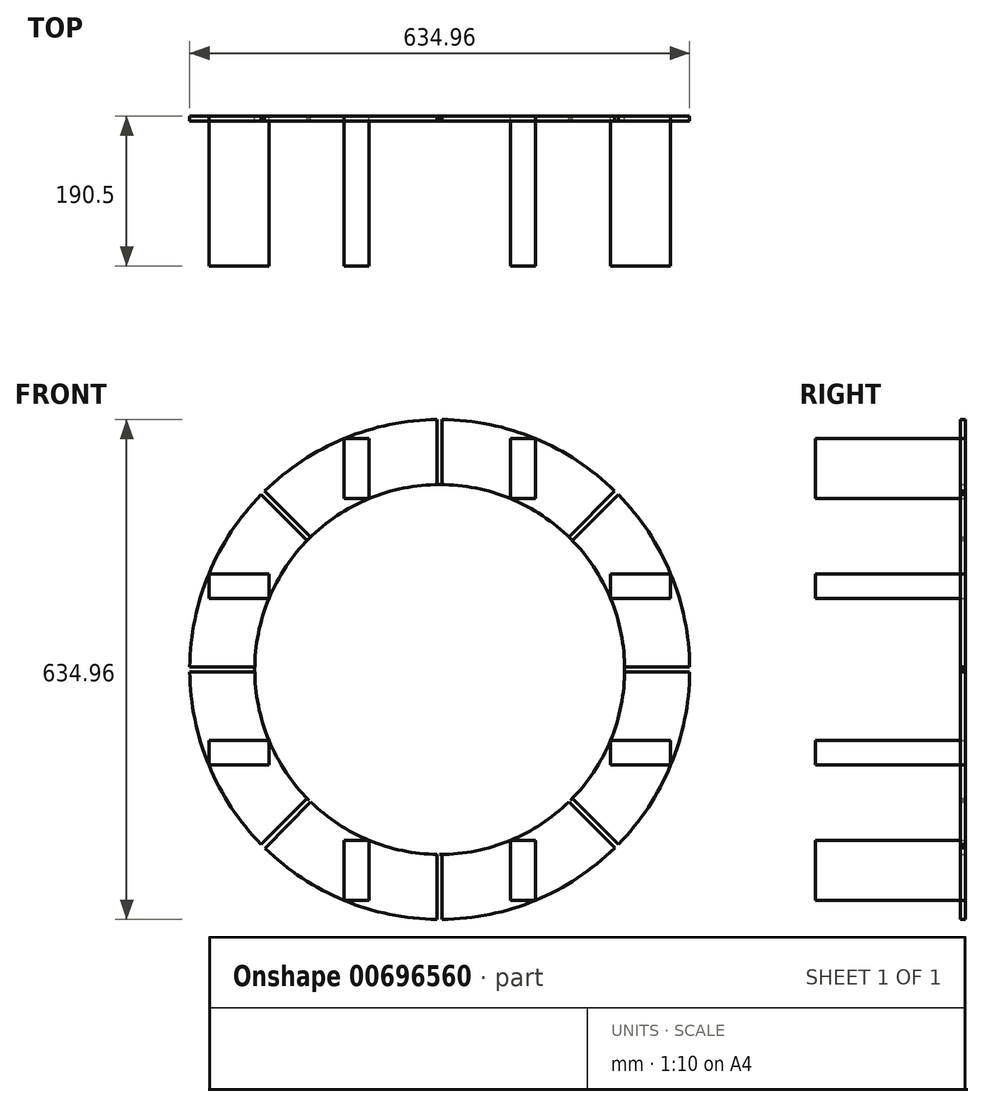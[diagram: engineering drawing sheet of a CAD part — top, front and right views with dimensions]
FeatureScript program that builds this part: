
annotation { "Feature Type Name" : "Feature", "Feature Type Description" : "" }
export const myFeature = defineFeature(function(context is Context, id is Id, definition is map)
    precondition{}
    {
        {
            var Q0;
            Q0=qCreatedBy(makeId("Front.planeOp"),FACE);
            var sketch = newSketch(context, id + "F0", { "sketchPlane" : qUnion([Q0])});
            skCircle(sketch, "E0", {"center": v(0, 0) * mm, "radius": 234.95 * mm});
            skCircle(sketch, "E1", {"center": v(0, 0) * mm, "radius": 317.5 * mm});
            skLineSegment(sketch, "E2", {"start": v(317.48, 0) * mm, "end": v(317.5, 0) * mm});
            skLineSegment(sketch, "E3", {"start": v(317.5, 0) * mm, "end": v(317.48, 0) * mm});
            skLineSegment(sketch, "E4", {"start": v(-317.48, 0) * mm, "end": v(-317.5, 0) * mm});
            skLineSegment(sketch, "E5", {"start": v(0, 317.5) * mm, "end": v(0, 317.5) * mm});
            skLineSegment(sketch, "E6", {"start": v(0, -317.48) * mm, "end": v(0, -317.5) * mm});
            skLineSegment(sketch, "E7.bottom", {"start": v(-317.5, 0) * mm, "end": v(-317.48, 0) * mm});
            skLineSegment(sketch, "E8", {"start": v(-224.5, 224.5) * mm, "end": v(-224.5, 224.5) * mm});
            skLineSegment(sketch, "E9", {"start": v(224.5, 224.5) * mm, "end": v(224.5, 224.5) * mm});
            skLineSegment(sketch, "E10", {"start": v(-224.5, -224.5) * mm, "end": v(-224.5, -224.5) * mm});
            skLineSegment(sketch, "E11", {"start": v(224.5, -224.5) * mm, "end": v(224.5, -224.5) * mm});
            skLineSegment(sketch, "E12", {"start": v(-166.13, -166.13) * mm, "end": v(-163.87, -168.36) * mm});
            skLineSegment(sketch, "E13", {"start": v(-166.13, -166.13) * mm, "end": v(-168.38, -163.89) * mm});
            skLineSegment(sketch, "E14", {"start": v(-168.38, -163.89) * mm, "end": v(-226.74, -222.25) * mm});
            skLineSegment(sketch, "E15", {"start": v(-163.87, -168.36) * mm, "end": v(-221.85, -227.13) * mm});
            skLineSegment(sketch, "E16", {"start": v(-221.85, -227.13) * mm, "end": v(-226.74, -222.25) * mm});
            skLineSegment(sketch, "E17", {"start": v(0, -234.95) * mm, "end": v(-3.17, -234.93) * mm});
            skLineSegment(sketch, "E18", {"start": v(0, -234.95) * mm, "end": v(3.18, -234.95) * mm});
            skLineSegment(sketch, "E19", {"start": v(-3.17, -234.93) * mm, "end": v(-3.17, -317.48) * mm});
            skLineSegment(sketch, "E20", {"start": v(3.18, -234.95) * mm, "end": v(3.18, -317.48) * mm});
            skLineSegment(sketch, "E21", {"start": v(3.18, -317.48) * mm, "end": v(-3.17, -317.48) * mm});
            skLineSegment(sketch, "E22", {"start": v(166.13, -166.13) * mm, "end": v(163.74, -168.22) * mm});
            skLineSegment(sketch, "E23", {"start": v(166.13, -166.13) * mm, "end": v(168.38, -163.89) * mm});
            skLineSegment(sketch, "E24", {"start": v(163.74, -168.22) * mm, "end": v(222.26, -226.73) * mm});
            skLineSegment(sketch, "E25", {"start": v(168.38, -163.89) * mm, "end": v(226.74, -222.25) * mm});
            skLineSegment(sketch, "E26", {"start": v(226.74, -222.25) * mm, "end": v(222.26, -226.73) * mm});
            skLineSegment(sketch, "E27", {"start": v(234.95, 0) * mm, "end": v(234.95, -3.17) * mm});
            skLineSegment(sketch, "E28", {"start": v(234.95, 0) * mm, "end": v(234.95, 3.18) * mm});
            skLineSegment(sketch, "E29", {"start": v(234.95, 3.18) * mm, "end": v(317.48, 3.18) * mm});
            skLineSegment(sketch, "E30", {"start": v(317.48, 3.18) * mm, "end": v(317.48, -3.18) * mm});
            skLineSegment(sketch, "E31", {"start": v(317.48, -3.18) * mm, "end": v(234.95, -3.17) * mm});
            skLineSegment(sketch, "E32", {"start": v(166.13, 166.13) * mm, "end": v(168.38, 163.89) * mm});
            skLineSegment(sketch, "E33", {"start": v(166.13, 166.13) * mm, "end": v(163.89, 168.38) * mm});
            skLineSegment(sketch, "E34", {"start": v(168.38, 163.89) * mm, "end": v(226.74, 222.25) * mm});
            skLineSegment(sketch, "E35", {"start": v(226.74, 222.25) * mm, "end": v(222.25, 226.74) * mm});
            skLineSegment(sketch, "E36", {"start": v(222.25, 226.74) * mm, "end": v(163.89, 168.38) * mm});
            skLineSegment(sketch, "E37", {"start": v(0, 234.95) * mm, "end": v(3.17, 234.95) * mm});
            skLineSegment(sketch, "E38", {"start": v(0, 234.95) * mm, "end": v(-3.17, 234.95) * mm});
            skLineSegment(sketch, "E39", {"start": v(-3.17, 234.95) * mm, "end": v(-3.17, 317.48) * mm});
            skLineSegment(sketch, "E40", {"start": v(-3.17, 317.48) * mm, "end": v(3.17, 317.5) * mm});
            skLineSegment(sketch, "E41", {"start": v(3.17, 317.5) * mm, "end": v(3.17, 234.95) * mm});
            skLineSegment(sketch, "E42", {"start": v(-166.13, 166.13) * mm, "end": v(-168.38, 163.89) * mm});
            skLineSegment(sketch, "E43", {"start": v(-166.13, 166.13) * mm, "end": v(-163.89, 168.38) * mm});
            skLineSegment(sketch, "E44", {"start": v(-168.38, 163.89) * mm, "end": v(-226.74, 222.25) * mm});
            skLineSegment(sketch, "E45", {"start": v(-226.74, 222.25) * mm, "end": v(-222.25, 226.74) * mm});
            skLineSegment(sketch, "E46", {"start": v(-222.25, 226.74) * mm, "end": v(-163.89, 168.38) * mm});
            skLineSegment(sketch, "E47", {"start": v(-234.95, 0) * mm, "end": v(-234.95, -3.18) * mm});
            skLineSegment(sketch, "E48", {"start": v(-234.95, 0) * mm, "end": v(-234.95, 3.17) * mm});
            skLineSegment(sketch, "E49", {"start": v(-234.95, 3.17) * mm, "end": v(-317.48, 3.17) * mm});
            skLineSegment(sketch, "E50", {"start": v(-317.48, 3.17) * mm, "end": v(-317.48, -3.18) * mm});
            skLineSegment(sketch, "E51", {"start": v(-317.48, -3.17) * mm, "end": v(-234.95, -3.18) * mm});
            skLineSegment(sketch, "E52", {"start": v(-163.89, 168.38) * mm, "end": v(-3.18, 234.95) * mm});
            skLineSegment(sketch, "E53", {"start": v(3.17, 234.95) * mm, "end": v(163.89, 168.38) * mm});
            skLineSegment(sketch, "E54", {"start": v(168.38, 163.89) * mm, "end": v(234.95, 3.18) * mm});
            skLineSegment(sketch, "E55", {"start": v(234.95, -3.18) * mm, "end": v(168.38, -163.89) * mm});
            skLineSegment(sketch, "E56", {"start": v(3.18, -234.95) * mm, "end": v(163.74, -168.22) * mm});
            skLineSegment(sketch, "E57", {"start": v(-3.17, -234.93) * mm, "end": v(-163.87, -168.36) * mm});
            skLineSegment(sketch, "E58", {"start": v(-168.38, -163.89) * mm, "end": v(-234.95, -3.18) * mm});
            skLineSegment(sketch, "E59", {"start": v(-234.95, 3.17) * mm, "end": v(-168.38, 163.89) * mm});
            skLineSegment(sketch, "E60", {"start": v(201.66, -83.53) * mm, "end": v(293.33, -121.5) * mm});
            skLineSegment(sketch, "E61", {"start": v(83.46, -201.58) * mm, "end": v(121.58, -293.3) * mm});
            skLineSegment(sketch, "E62", {"start": v(-201.66, -83.53) * mm, "end": v(-293.33, -121.5) * mm});
            skLineSegment(sketch, "E63", {"start": v(-201.66, 83.53) * mm, "end": v(-293.33, 121.5) * mm});
            skLineSegment(sketch, "E64", {"start": v(-83.53, 201.66) * mm, "end": v(-121.5, 293.33) * mm});
            skLineSegment(sketch, "E65", {"start": v(83.53, 201.66) * mm, "end": v(121.5, 293.33) * mm});
            skLineSegment(sketch, "E66", {"start": v(201.66, 83.53) * mm, "end": v(293.33, 121.5) * mm});
            skLineSegment(sketch, "E67.bottom", {"start": v(121.5, 293.33) * mm, "end": v(89.91, 293.33) * mm});
            skLineSegment(sketch, "E67.top", {"start": v(121.5, 217.07) * mm, "end": v(89.91, 217.07) * mm});
            skLineSegment(sketch, "E67.left", {"start": v(121.5, 293.33) * mm, "end": v(121.5, 217.07) * mm});
            skLineSegment(sketch, "E67.right", {"start": v(89.91, 293.33) * mm, "end": v(89.91, 217.07) * mm});
            skLineSegment(sketch, "E68.bottom", {"start": v(293.33, 121.5) * mm, "end": v(217.07, 121.5) * mm});
            skLineSegment(sketch, "E68.top", {"start": v(293.33, 89.91) * mm, "end": v(217.07, 89.91) * mm});
            skLineSegment(sketch, "E68.left", {"start": v(293.33, 121.5) * mm, "end": v(293.33, 89.91) * mm});
            skLineSegment(sketch, "E68.right", {"start": v(217.07, 121.5) * mm, "end": v(217.07, 89.91) * mm});
            skLineSegment(sketch, "E69.bottom", {"start": v(293.33, -121.5) * mm, "end": v(217.07, -121.5) * mm});
            skLineSegment(sketch, "E69.top", {"start": v(293.33, -89.91) * mm, "end": v(217.07, -89.91) * mm});
            skLineSegment(sketch, "E69.left", {"start": v(293.33, -121.5) * mm, "end": v(293.33, -89.91) * mm});
            skLineSegment(sketch, "E69.right", {"start": v(217.07, -121.5) * mm, "end": v(217.07, -89.91) * mm});
            skLineSegment(sketch, "E70.bottom", {"start": v(121.58, -293.3) * mm, "end": v(89.9, -293.3) * mm});
            skLineSegment(sketch, "E70.top", {"start": v(121.58, -217.07) * mm, "end": v(89.9, -217.07) * mm});
            skLineSegment(sketch, "E70.left", {"start": v(121.58, -293.3) * mm, "end": v(121.58, -217.07) * mm});
            skLineSegment(sketch, "E70.right", {"start": v(89.9, -293.3) * mm, "end": v(89.9, -217.07) * mm});
            skLineSegment(sketch, "E71.bottom", {"start": v(-293.33, -121.5) * mm, "end": v(-217.07, -121.5) * mm});
            skLineSegment(sketch, "E71.top", {"start": v(-293.33, -89.91) * mm, "end": v(-217.07, -89.91) * mm});
            skLineSegment(sketch, "E71.left", {"start": v(-293.33, -121.5) * mm, "end": v(-293.33, -89.91) * mm});
            skLineSegment(sketch, "E71.right", {"start": v(-217.07, -121.5) * mm, "end": v(-217.07, -89.91) * mm});
            skLineSegment(sketch, "E72.bottom", {"start": v(-293.33, 121.5) * mm, "end": v(-217.07, 121.5) * mm});
            skLineSegment(sketch, "E72.top", {"start": v(-293.33, 89.91) * mm, "end": v(-217.07, 89.91) * mm});
            skLineSegment(sketch, "E72.left", {"start": v(-293.33, 121.5) * mm, "end": v(-293.33, 89.91) * mm});
            skLineSegment(sketch, "E72.right", {"start": v(-217.07, 121.5) * mm, "end": v(-217.07, 89.91) * mm});
            skLineSegment(sketch, "E73.bottom", {"start": v(-121.5, 293.33) * mm, "end": v(-89.91, 293.33) * mm});
            skLineSegment(sketch, "E73.top", {"start": v(-121.5, 217.07) * mm, "end": v(-89.91, 217.07) * mm});
            skLineSegment(sketch, "E73.left", {"start": v(-121.5, 293.33) * mm, "end": v(-121.5, 217.07) * mm});
            skLineSegment(sketch, "E73.right", {"start": v(-89.91, 293.33) * mm, "end": v(-89.91, 217.07) * mm});
            skLineSegment(sketch, "E74", {"start": v(-83.52, -201.65) * mm, "end": v(-121.5, -293.33) * mm});
            skLineSegment(sketch, "E75.bottom", {"start": v(-121.5, -293.33) * mm, "end": v(-89.91, -293.33) * mm});
            skLineSegment(sketch, "E75.top", {"start": v(-121.5, -217.07) * mm, "end": v(-89.91, -217.07) * mm});
            skLineSegment(sketch, "E75.left", {"start": v(-121.5, -293.33) * mm, "end": v(-121.5, -217.07) * mm});
            skLineSegment(sketch, "E75.right", {"start": v(-89.91, -293.33) * mm, "end": v(-89.91, -217.07) * mm});
            skSolve(sketch);
        }
        {
            var Q0;
            Q0=makeQuery(id+"F0.imprint","IMPRINT",FACE,{"disambiguationData":[TD([[makeQuery(id+"F0.imprint","IMPRINT",EDGE,{"derivedFrom":sQuery(id+"F0.wireOp",EDGE,"E0")}),-1.0]])]});
            var Q1;
            {var subQ1=sQuery(id+"F0.wireOp",EDGE,"E13");Q1=makeQuery(id+"F0.imprint","IMPRINT",FACE,{"disambiguationData":[TD([[makeQuery(id+"F0.imprint","IMPRINT",EDGE,{"derivedFrom":subQ1}),-1.0]])]});}
            var Q2;
            {var subQ3=sQuery(id+"F0.wireOp",EDGE,"E42");Q2=makeQuery(id+"F0.imprint","IMPRINT",FACE,{"disambiguationData":[TD([[makeQuery(id+"F0.imprint","IMPRINT",EDGE,{"derivedFrom":subQ3}),1.0]])]});}
            var Q3;
            {var subQ0=sQuery(id+"F0.wireOp",EDGE,"E38");Q3=makeQuery(id+"F0.imprint","IMPRINT",FACE,{"disambiguationData":[TD([[makeQuery(id+"F0.imprint","IMPRINT",EDGE,{"derivedFrom":subQ0}),1.0]])]});}
            var Q4;
            {var subQ1=sQuery(id+"F0.wireOp",EDGE,"E33");Q4=makeQuery(id+"F0.imprint","IMPRINT",FACE,{"disambiguationData":[TD([[makeQuery(id+"F0.imprint","IMPRINT",EDGE,{"derivedFrom":subQ1}),1.0]])]});}
            var Q5;
            {var subQ0=sQuery(id+"F0.wireOp",EDGE,"E28");Q5=makeQuery(id+"F0.imprint","IMPRINT",FACE,{"disambiguationData":[TD([[makeQuery(id+"F0.imprint","IMPRINT",EDGE,{"derivedFrom":subQ0}),1.0]])]});}
            var Q6;
            {var subQ0=sQuery(id+"F0.wireOp",EDGE,"E23");Q6=makeQuery(id+"F0.imprint","IMPRINT",FACE,{"disambiguationData":[TD([[makeQuery(id+"F0.imprint","IMPRINT",EDGE,{"derivedFrom":subQ0}),1.0]])]});}
            var Q7;
            {var subQ0=sQuery(id+"F0.wireOp",EDGE,"E18");Q7=makeQuery(id+"F0.imprint","IMPRINT",FACE,{"disambiguationData":[TD([[makeQuery(id+"F0.imprint","IMPRINT",EDGE,{"derivedFrom":subQ0}),1.0]])]});}
            var Q8;
            {var subQ1=sQuery(id+"F0.wireOp",EDGE,"E44");Q8=makeQuery(id+"F0.imprint","IMPRINT",FACE,{"disambiguationData":[TD([[makeQuery(id+"F0.imprint","IMPRINT",EDGE,{"derivedFrom":subQ1}),1.0]])]});}
            var Q9;
            {var subQ0=sQuery(id+"F0.wireOp",EDGE,"E49");Q9=makeQuery(id+"F0.imprint","IMPRINT",FACE,{"disambiguationData":[TD([[makeQuery(id+"F0.imprint","IMPRINT",EDGE,{"derivedFrom":subQ0}),-1.0]])]});}
            var Q10;
            {var subQ1=sQuery(id+"F0.wireOp",EDGE,"E51");Q10=makeQuery(id+"F0.imprint","IMPRINT",FACE,{"disambiguationData":[TD([[makeQuery(id+"F0.imprint","IMPRINT",EDGE,{"derivedFrom":subQ1}),-1.0]])]});}
            var Q11;
            {var subQ1=sQuery(id+"F0.wireOp",EDGE,"E14");Q11=makeQuery(id+"F0.imprint","IMPRINT",FACE,{"disambiguationData":[TD([[makeQuery(id+"F0.imprint","IMPRINT",EDGE,{"derivedFrom":subQ1}),-1.0]])]});}
            var Q12;
            {var subQ1=sQuery(id+"F0.wireOp",EDGE,"E15");Q12=makeQuery(id+"F0.imprint","IMPRINT",FACE,{"disambiguationData":[TD([[makeQuery(id+"F0.imprint","IMPRINT",EDGE,{"derivedFrom":subQ1}),1.0]])]});}
            var Q13;
            {var subQ0=sQuery(id+"F0.wireOp",EDGE,"E19");Q13=makeQuery(id+"F0.imprint","IMPRINT",FACE,{"disambiguationData":[TD([[makeQuery(id+"F0.imprint","IMPRINT",EDGE,{"derivedFrom":subQ0}),-1.0]])]});}
            var Q14;
            {var subQ0=sQuery(id+"F0.wireOp",EDGE,"E20");Q14=makeQuery(id+"F0.imprint","IMPRINT",FACE,{"disambiguationData":[TD([[makeQuery(id+"F0.imprint","IMPRINT",EDGE,{"derivedFrom":subQ0}),1.0]])]});}
            var Q15;
            {var subQ0=sQuery(id+"F0.wireOp",EDGE,"E70.top");Q15=makeQuery(id+"F0.imprint","IMPRINT",FACE,{"disambiguationData":[TD([[makeQuery(id+"F0.imprint","IMPRINT",EDGE,{"derivedFrom":subQ0}),-1.0]])]});}
            var Q16;
            {var subQ0=sQuery(id+"F0.wireOp",EDGE,"E25");Q16=makeQuery(id+"F0.imprint","IMPRINT",FACE,{"disambiguationData":[TD([[makeQuery(id+"F0.imprint","IMPRINT",EDGE,{"derivedFrom":subQ0}),1.0]])]});}
            var Q17;
            {var subQ1=sQuery(id+"F0.wireOp",EDGE,"E31");Q17=makeQuery(id+"F0.imprint","IMPRINT",FACE,{"disambiguationData":[TD([[makeQuery(id+"F0.imprint","IMPRINT",EDGE,{"derivedFrom":subQ1}),1.0]])]});}
            var Q18;
            {var subQ1=sQuery(id+"F0.wireOp",EDGE,"E29");Q18=makeQuery(id+"F0.imprint","IMPRINT",FACE,{"disambiguationData":[TD([[makeQuery(id+"F0.imprint","IMPRINT",EDGE,{"derivedFrom":subQ1}),1.0]])]});}
            var Q19;
            {var subQ0=sQuery(id+"F0.wireOp",EDGE,"E34");Q19=makeQuery(id+"F0.imprint","IMPRINT",FACE,{"disambiguationData":[TD([[makeQuery(id+"F0.imprint","IMPRINT",EDGE,{"derivedFrom":subQ0}),-1.0]])]});}
            var Q20;
            {var subQ1=sQuery(id+"F0.wireOp",EDGE,"E36");Q20=makeQuery(id+"F0.imprint","IMPRINT",FACE,{"disambiguationData":[TD([[makeQuery(id+"F0.imprint","IMPRINT",EDGE,{"derivedFrom":subQ1}),-1.0]])]});}
            var Q21;
            {var subQ5=sQuery(id+"F0.wireOp",EDGE,"E67.bottom");Q21=makeQuery(id+"F0.imprint","IMPRINT",FACE,{"disambiguationData":[TD([[makeQuery(id+"F0.imprint","IMPRINT",EDGE,{"derivedFrom":subQ5}),-1.0]])]});}
            var Q22;
            {var subQ0=sQuery(id+"F0.wireOp",EDGE,"E39");Q22=makeQuery(id+"F0.imprint","IMPRINT",FACE,{"disambiguationData":[TD([[makeQuery(id+"F0.imprint","IMPRINT",EDGE,{"derivedFrom":subQ0}),1.0]])]});}
            var Q23;
            {var subQ1=sQuery(id+"F0.wireOp",EDGE,"E46");Q23=makeQuery(id+"F0.imprint","IMPRINT",FACE,{"disambiguationData":[TD([[makeQuery(id+"F0.imprint","IMPRINT",EDGE,{"derivedFrom":subQ1}),1.0]])]});}
            extrude(context, id + "F1", {"entities" : qUnion([Q0, Q1, Q2, Q3, Q4, Q5, Q6, Q7, Q8, Q9, Q10, Q11, Q12, Q13, Q14, Q15, Q16, Q17, Q18, Q19, Q20, Q21, Q22, Q23]), "depth" : 6.35 * mm, "offsetDistance" : 25.4 * mm});
        }
        {
            var Q0;
            {var subQ2=sQuery(id+"F0.wireOp",EDGE,"E72.top");Q0=makeQuery(id+"F0.imprint","IMPRINT",FACE,{"disambiguationData":[TD([[makeQuery(id+"F0.imprint","IMPRINT",EDGE,{"derivedFrom":subQ2}),1.0]])]});}
            var Q1;
            {var subQ0=sQuery(id+"F0.wireOp",EDGE,"E72.bottom");Q1=makeQuery(id+"F0.imprint","IMPRINT",FACE,{"disambiguationData":[TD([[makeQuery(id+"F0.imprint","IMPRINT",EDGE,{"derivedFrom":subQ0}),-1.0]])]});}
            var Q2;
            {var subQ2=sQuery(id+"F0.wireOp",EDGE,"E73.top");Q2=makeQuery(id+"F0.imprint","IMPRINT",FACE,{"disambiguationData":[TD([[makeQuery(id+"F0.imprint","IMPRINT",EDGE,{"derivedFrom":subQ2}),1.0]])]});}
            var Q3;
            {var subQ0=sQuery(id+"F0.wireOp",EDGE,"E73.bottom");Q3=makeQuery(id+"F0.imprint","IMPRINT",FACE,{"disambiguationData":[TD([[makeQuery(id+"F0.imprint","IMPRINT",EDGE,{"derivedFrom":subQ0}),-1.0]])]});}
            var Q4;
            {var subQ0=sQuery(id+"F0.wireOp",EDGE,"E67.bottom");Q4=makeQuery(id+"F0.imprint","IMPRINT",FACE,{"disambiguationData":[TD([[makeQuery(id+"F0.imprint","IMPRINT",EDGE,{"derivedFrom":subQ0}),1.0]])]});}
            var Q5;
            {var subQ2=sQuery(id+"F0.wireOp",EDGE,"E67.top");Q5=makeQuery(id+"F0.imprint","IMPRINT",FACE,{"disambiguationData":[TD([[makeQuery(id+"F0.imprint","IMPRINT",EDGE,{"derivedFrom":subQ2}),-1.0]])]});}
            var Q6;
            {var subQ0=sQuery(id+"F0.wireOp",EDGE,"E68.bottom");Q6=makeQuery(id+"F0.imprint","IMPRINT",FACE,{"disambiguationData":[TD([[makeQuery(id+"F0.imprint","IMPRINT",EDGE,{"derivedFrom":subQ0}),1.0]])]});}
            var Q7;
            {var subQ2=sQuery(id+"F0.wireOp",EDGE,"E68.top");Q7=makeQuery(id+"F0.imprint","IMPRINT",FACE,{"disambiguationData":[TD([[makeQuery(id+"F0.imprint","IMPRINT",EDGE,{"derivedFrom":subQ2}),-1.0]])]});}
            var Q8;
            {var subQ2=sQuery(id+"F0.wireOp",EDGE,"E69.top");Q8=makeQuery(id+"F0.imprint","IMPRINT",FACE,{"disambiguationData":[TD([[makeQuery(id+"F0.imprint","IMPRINT",EDGE,{"derivedFrom":subQ2}),1.0]])]});}
            var Q9;
            {var subQ0=sQuery(id+"F0.wireOp",EDGE,"E69.bottom");Q9=makeQuery(id+"F0.imprint","IMPRINT",FACE,{"disambiguationData":[TD([[makeQuery(id+"F0.imprint","IMPRINT",EDGE,{"derivedFrom":subQ0}),-1.0]])]});}
            var Q10;
            {var subQ2=sQuery(id+"F0.wireOp",EDGE,"E70.top");Q10=makeQuery(id+"F0.imprint","IMPRINT",FACE,{"disambiguationData":[TD([[makeQuery(id+"F0.imprint","IMPRINT",EDGE,{"derivedFrom":subQ2}),1.0]])]});}
            var Q11;
            {var subQ0=sQuery(id+"F0.wireOp",EDGE,"E70.bottom");Q11=makeQuery(id+"F0.imprint","IMPRINT",FACE,{"disambiguationData":[TD([[makeQuery(id+"F0.imprint","IMPRINT",EDGE,{"derivedFrom":subQ0}),-1.0]])]});}
            var Q12;
            {var subQ0=sQuery(id+"F0.wireOp",EDGE,"E75.bottom");Q12=makeQuery(id+"F0.imprint","IMPRINT",FACE,{"disambiguationData":[TD([[makeQuery(id+"F0.imprint","IMPRINT",EDGE,{"derivedFrom":subQ0}),1.0]])]});}
            var Q13;
            {var subQ2=sQuery(id+"F0.wireOp",EDGE,"E75.top");Q13=makeQuery(id+"F0.imprint","IMPRINT",FACE,{"disambiguationData":[TD([[makeQuery(id+"F0.imprint","IMPRINT",EDGE,{"derivedFrom":subQ2}),-1.0]])]});}
            var Q14;
            {var subQ0=sQuery(id+"F0.wireOp",EDGE,"E71.bottom");Q14=makeQuery(id+"F0.imprint","IMPRINT",FACE,{"disambiguationData":[TD([[makeQuery(id+"F0.imprint","IMPRINT",EDGE,{"derivedFrom":subQ0}),1.0]])]});}
            var Q15;
            {var subQ2=sQuery(id+"F0.wireOp",EDGE,"E71.top");Q15=makeQuery(id+"F0.imprint","IMPRINT",FACE,{"disambiguationData":[TD([[makeQuery(id+"F0.imprint","IMPRINT",EDGE,{"derivedFrom":subQ2}),-1.0]])]});}
            extrude(context, id + "F2", {"entities" : qUnion([Q0, Q1, Q2, Q3, Q4, Q5, Q6, Q7, Q8, Q9, Q10, Q11, Q12, Q13, Q14, Q15]), "depth" : 190.5 * mm, "offsetDistance" : 25.4 * mm});
        }
    });
